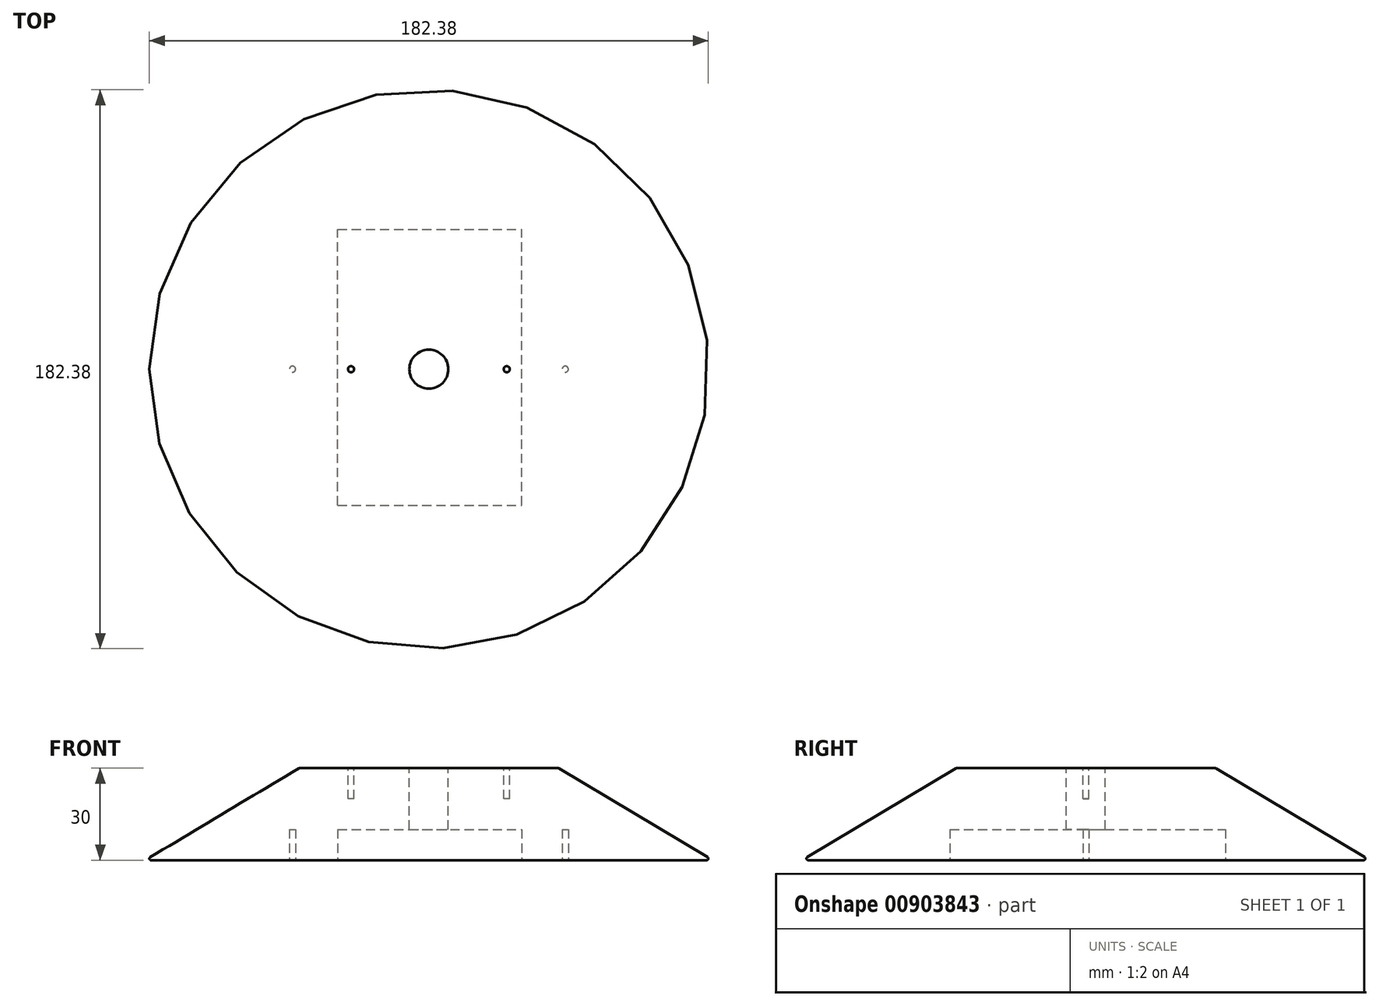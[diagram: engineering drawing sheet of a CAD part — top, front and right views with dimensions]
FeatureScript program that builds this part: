
annotation { "Feature Type Name" : "Feature", "Feature Type Description" : "" }
export const myFeature = defineFeature(function(context is Context, id is Id, definition is map)
    precondition{}
    {
        {
            var Q0;
            Q0=qCreatedBy(makeId("Front.planeOp"),FACE);
            var sketch = newSketch(context, id + "F0", { "sketchPlane" : qUnion([Q0])});
            skLineSegment(sketch, "E0.bottom", {"start": v(0, 0) * mm, "end": v(92.5, 0) * mm});
            skLineSegment(sketch, "E0.top", {"start": v(0, 30) * mm, "end": v(42.4, 30) * mm});
            skLineSegment(sketch, "E0.left", {"start": v(0, 0) * mm, "end": v(0, 30) * mm});
            skLineSegment(sketch, "E1", {"start": v(92.5, 0) * mm, "end": v(42.4, 30) * mm});
            skPoint(sketch, "E0.right.end.orphan", {"position": v(92.5, 30) * mm});
            skSolve(sketch);
        }
        {
            var Q0;
            Q0 = qSketchRegion(id + "F0", true);
            var Q1;
            Q1=sQuery(id+"F0.wireOp",EDGE,"E0.left");
            revolve(context, id + "F1", {"surfaceOperationType" : NewSurfaceOperationType.NEW, "entities" : qUnion([Q0]), "axis" : qUnion([Q1]), "revolveType" : RevolveType.FULL});
        }
        {
            var Q0;
            Q0=makeQuery(id+"F1.opRevolve","SWEPT_FACE",FACE,{"disambiguationData":[OSD([sQuery(id+"F0.wireOp",EDGE,"E0.top")])]});
            var sketch = newSketch(context, id + "F2", { "sketchPlane" : qUnion([Q0])});
            skCircle(sketch, "E2", {"center": v(0, 0) * mm, "radius": 6.35 * mm});
            skSolve(sketch);
        }
        {
            var Q0;
            Q0=sQuery(id+"F2.wireOp",VERTEX,"E2.center");
            var Q1;
            Q1=makeQuery(id+"F1.opRevolve","SWEPT_BODY",BODY,{"disambiguationData":[OSD([sQuery(id+"F0.wireOp",EDGE,"E0.bottom"),sQuery(id+"F0.wireOp",EDGE,"E0.left"),sQuery(id+"F0.wireOp",EDGE,"E0.top"),sQuery(id+"F0.wireOp",EDGE,"E1")])]});
            hole(context, id + "F3", {"style" : HoleStyle.SIMPLE, "endStyle" : HoleEndStyle.THROUGH, "holeDiameter" : 12.7 * mm, "majorDiameter" : 5 * mm, "isTappedThrough" : true, "tappedDepth" : 12 * mm, "tapClearance" : 3, "locations" : qUnion([Q0]), "scope" : qUnion([Q1])});
        }
        {
            var Q0;
            Q0=makeQuery(id+"F1.opRevolve","SWEPT_FACE",FACE,{"disambiguationData":[OSD([sQuery(id+"F0.wireOp",EDGE,"E0.bottom")])]});
            var sketch = newSketch(context, id + "F4", { "sketchPlane" : qUnion([Q0])});
            skLineSegment(sketch, "E3.bottom", {"start": v(-29.77, 44.4) * mm, "end": v(30.23, 44.4) * mm});
            skLineSegment(sketch, "E3.top", {"start": v(-29.77, -45.6) * mm, "end": v(30.23, -45.6) * mm});
            skLineSegment(sketch, "E3.left", {"start": v(-29.77, 44.4) * mm, "end": v(-29.77, -45.6) * mm});
            skLineSegment(sketch, "E3.right", {"start": v(30.23, 44.4) * mm, "end": v(30.23, -45.6) * mm});
            skSolve(sketch);
        }
        {
            var Q0;
            Q0=makeQuery(id+"F4.imprint","IMPRINT",FACE,{"disambiguationData":[TD([[makeQuery(id+"F4.imprint","IMPRINT",EDGE,{"derivedFrom":sQuery(id+"F4.wireOp",EDGE,"E3.bottom")}),-1.0]])]});
            extrude(context, id + "F5", {"entities" : qUnion([Q0]), "operationType" : NewBodyOperationType.REMOVE, "oppositeDirection" : true, "depth" : 10 * mm, "offsetDistance" : 25 * mm});
        }
        {
            var Q0;
            Q0=makeQuery(id+"F1.opRevolve","SWEPT_FACE",FACE,{"disambiguationData":[OSD([sQuery(id+"F0.wireOp",EDGE,"E0.bottom")])]});
            var sketch = newSketch(context, id + "F6", { "sketchPlane" : qUnion([Q0])});
            skCircle(sketch, "E4", {"center": v(-44.5, 0) * mm, "radius": 1 * mm});
            skCircle(sketch, "E5", {"center": v(44.5, 0) * mm, "radius": 1 * mm});
            skSolve(sketch);
        }
        {
            var Q0;
            Q0 = qSketchRegion(id + "F6", true);
            extrude(context, id + "F7", {"entities" : qUnion([Q0]), "operationType" : NewBodyOperationType.REMOVE, "oppositeDirection" : true, "depth" : 10 * mm, "offsetDistance" : 25 * mm});
        }
        {
            var Q0;
            Q0=makeQuery(id+"F1.opRevolve","SWEPT_FACE",FACE,{"disambiguationData":[OSD([sQuery(id+"F0.wireOp",EDGE,"E0.top")])]});
            var sketch = newSketch(context, id + "F8", { "sketchPlane" : qUnion([Q0])});
            skCircle(sketch, "E6", {"center": v(-25.4, 0) * mm, "radius": 1 * mm});
            skCircle(sketch, "E7", {"center": v(25.4, 0) * mm, "radius": 1 * mm});
            skSolve(sketch);
        }
        {
            var Q0;
            Q0 = qSketchRegion(id + "F8", true);
            extrude(context, id + "F9", {"entities" : qUnion([Q0]), "operationType" : NewBodyOperationType.REMOVE, "oppositeDirection" : true, "depth" : 10 * mm, "offsetDistance" : 25 * mm});
        }
        {
            var Q0;
            Q0=makeQuery(id+"F1.opRevolve","SWEPT_EDGE",EDGE,{"disambiguationData":[OSD([sQuery(id+"F0.wireOp",EDGE,"E0.bottom"),sQuery(id+"F0.wireOp",EDGE,"E1")])]});
            var Q1;
            Q1=makeQuery(id+"F1.opRevolve","SWEPT_EDGE",EDGE,{"disambiguationData":[OSD([sQuery(id+"F0.wireOp",EDGE,"E0.top"),sQuery(id+"F0.wireOp",EDGE,"E1")])]});
            fillet(context, id + "F10", {"entities" : qUnion([Q0, Q1]), "radius" : .5 * mm, "tangentPropagation" : true, "allowEdgeOverflow" : false});
        }
    });
